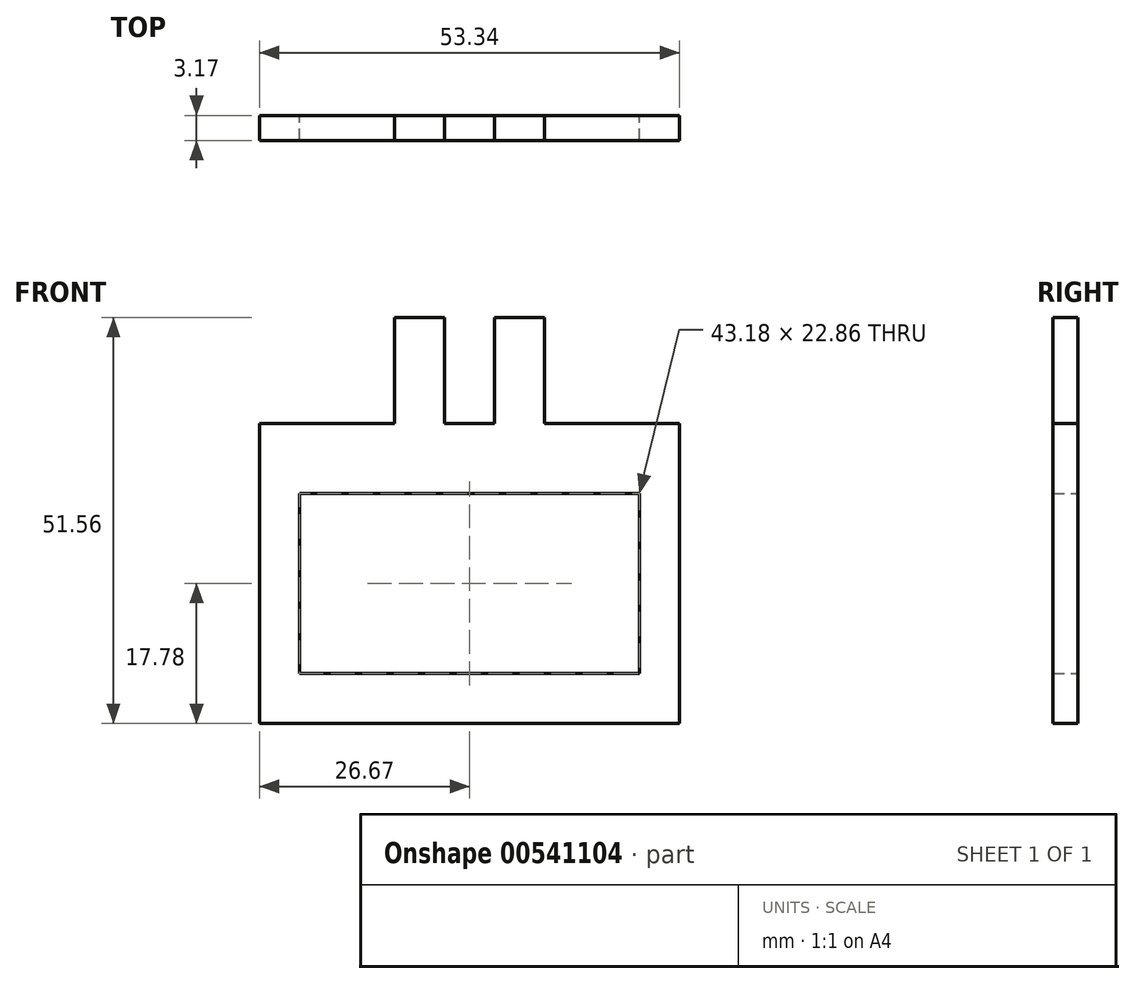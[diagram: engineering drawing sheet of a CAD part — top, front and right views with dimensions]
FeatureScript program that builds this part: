
annotation { "Feature Type Name" : "Feature", "Feature Type Description" : "" }
export const myFeature = defineFeature(function(context is Context, id is Id, definition is map)
    precondition{}
    {
        {
            var Q0;
            Q0=qCreatedBy(makeId("Front.planeOp"),FACE);
            var sketch = newSketch(context, id + "F0", { "sketchPlane" : qUnion([Q0])});
            skLineSegment(sketch, "E0", {"start": v(0, 0) * mm, "end": v(-26.67, 0) * mm});
            skLineSegment(sketch, "E1", {"start": v(-26.67, 0) * mm, "end": v(-26.67, 38.1) * mm});
            skLineSegment(sketch, "E2", {"start": v(-26.67, 38.1) * mm, "end": v(-9.53, 38.1) * mm});
            skLineSegment(sketch, "E3", {"start": v(-9.53, 38.1) * mm, "end": v(-9.53, 51.56) * mm});
            skLineSegment(sketch, "E4", {"start": v(-9.53, 51.56) * mm, "end": v(-3.18, 51.56) * mm});
            skLineSegment(sketch, "E5", {"start": v(-3.18, 51.56) * mm, "end": v(-3.18, 38.1) * mm});
            skLineSegment(sketch, "E6", {"start": v(-3.18, 38.1) * mm, "end": v(0, 38.1) * mm});
            skLineSegment(sketch, "E7.bottom", {"start": v(0, 6.35) * mm, "end": v(-21.59, 6.35) * mm});
            skLineSegment(sketch, "E7.top", {"start": v(0, 29.21) * mm, "end": v(-21.6, 29.21) * mm});
            skLineSegment(sketch, "E7.right", {"start": v(-21.59, 6.35) * mm, "end": v(-21.6, 29.21) * mm});
            skLineSegment(sketch, "E8.MirrorCS", {"start": v(3.18, 38.1) * mm, "end": v(0, 38.1) * mm});
            skLineSegment(sketch, "E9.MirrorCS", {"start": v(26.67, 0) * mm, "end": v(26.67, 38.1) * mm});
            skLineSegment(sketch, "E10.MirrorCS", {"start": v(21.59, 6.35) * mm, "end": v(21.6, 29.21) * mm});
            skLineSegment(sketch, "E11.MirrorCS", {"start": v(0, 29.21) * mm, "end": v(21.6, 29.21) * mm});
            skLineSegment(sketch, "E12.MirrorCS", {"start": v(0, 0) * mm, "end": v(26.67, 0) * mm});
            skLineSegment(sketch, "E13.MirrorCS", {"start": v(9.53, 51.56) * mm, "end": v(3.18, 51.56) * mm});
            skLineSegment(sketch, "E14.MirrorCS", {"start": v(0, 6.35) * mm, "end": v(21.59, 6.35) * mm});
            skLineSegment(sketch, "E15.MirrorCS", {"start": v(26.67, 38.1) * mm, "end": v(9.53, 38.1) * mm});
            skLineSegment(sketch, "E16.MirrorCS", {"start": v(9.53, 38.1) * mm, "end": v(9.53, 51.56) * mm});
            skLineSegment(sketch, "E17.MirrorCS", {"start": v(3.18, 51.56) * mm, "end": v(3.18, 38.1) * mm});
            skSolve(sketch);
        }
        {
            var Q0;
            Q0 = qSketchRegion(id + "F0", true);
            extrude(context, id + "F1", {"entities" : qUnion([Q0]), "depth" : 3.17 * mm, "offsetDistance" : 25.4 * mm});
        }
    });
